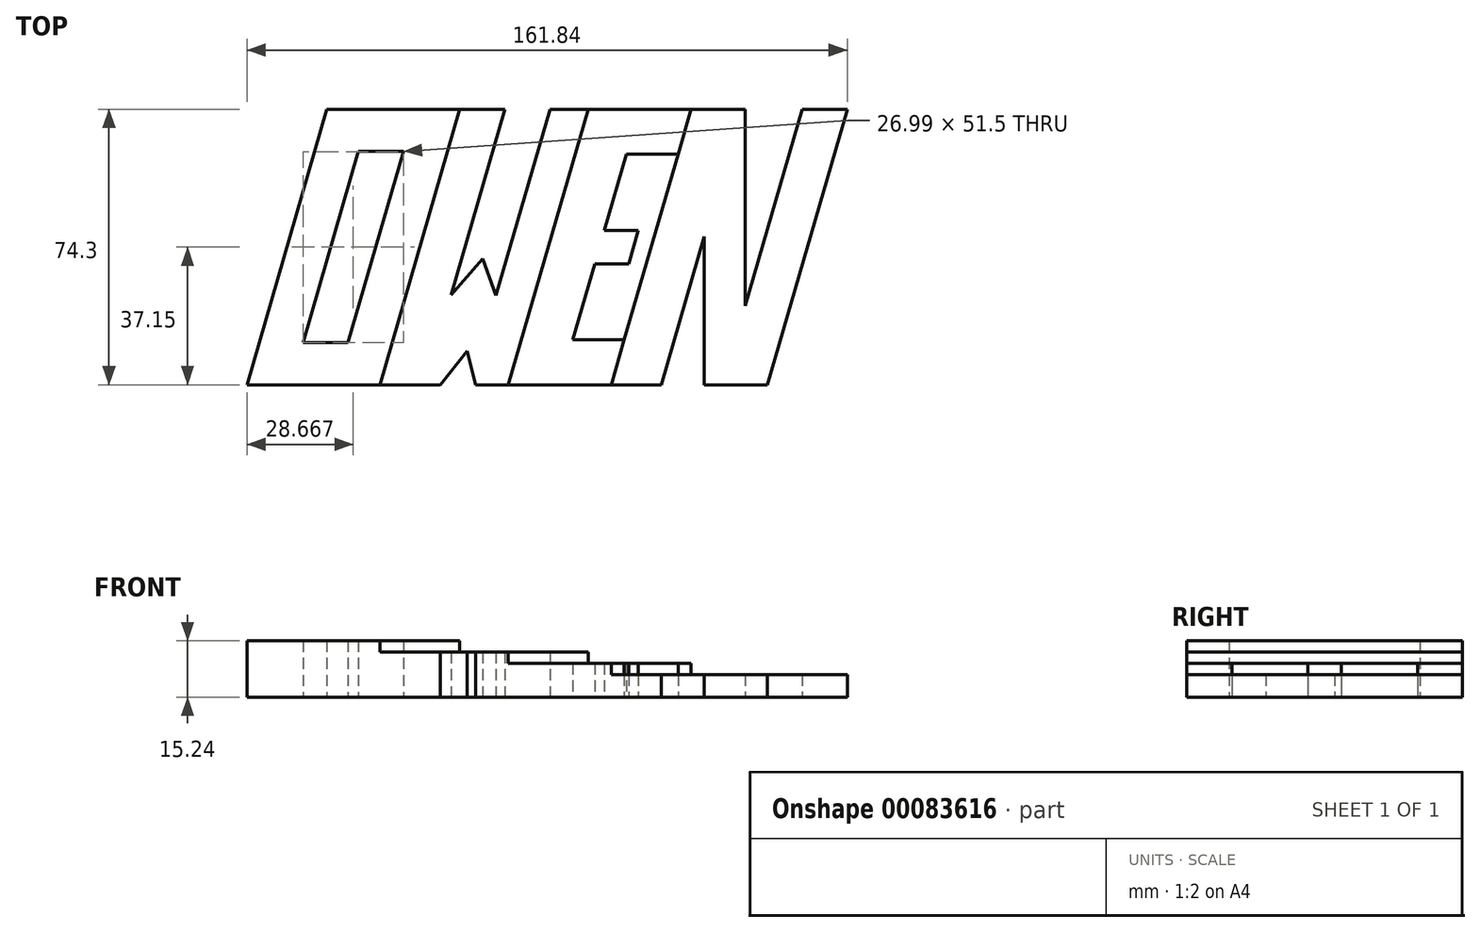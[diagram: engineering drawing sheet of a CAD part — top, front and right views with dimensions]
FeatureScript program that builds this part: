
annotation { "Feature Type Name" : "Feature", "Feature Type Description" : "" }
export const myFeature = defineFeature(function(context is Context, id is Id, definition is map)
    precondition{}
    {
        {
            var Q0;
            Q0=qCreatedBy(makeId("Top.planeOp"),FACE);
            var sketch = newSketch(context, id + "F0", { "sketchPlane" : qUnion([Q0])});
            skPoint(sketch, "E0.middle", {"position": v(0, 0) * mm});
            skLineSegment(sketch, "E1", {"start": v(-54.9, 37.15) * mm, "end": v(-76.4, -37.15) * mm});
            skLineSegment(sketch, "E2", {"start": v(-40.6, -37.15) * mm, "end": v(-19.08, 37.15) * mm});
            skLineSegment(sketch, "E3", {"start": v(-76.4, -37.15) * mm, "end": v(-40.6, -37.15) * mm});
            skLineSegment(sketch, "E4", {"start": v(-54.9, 37.15) * mm, "end": v(-19.08, 37.15) * mm});
            skLineSegment(sketch, "E5.0", {"start": v(-46.32, 25.75) * mm, "end": v(-61.24, -25.75) * mm});
            skLineSegment(sketch, "E5.1", {"start": v(-46.32, 25.75) * mm, "end": v(-34.25, 25.75) * mm});
            skLineSegment(sketch, "E5.2", {"start": v(-49.16, -25.75) * mm, "end": v(-34.25, 25.75) * mm});
            skLineSegment(sketch, "E5.3", {"start": v(-61.24, -25.75) * mm, "end": v(-49.16, -25.75) * mm});
            skLineSegment(sketch, "E6", {"start": v(-19.08, 37.15) * mm, "end": v(-6.88, 37.15) * mm});
            skLineSegment(sketch, "E7", {"start": v(-6.88, 37.15) * mm, "end": v(-21.37, -12.86) * mm});
            skLineSegment(sketch, "E8", {"start": v(-21.37, -12.86) * mm, "end": v(-12.84, -3.14) * mm});
            skLineSegment(sketch, "E9", {"start": v(-12.84, -3.14) * mm, "end": v(-9.23, -13.05) * mm});
            skLineSegment(sketch, "E10", {"start": v(-9.23, -13.05) * mm, "end": v(5.3, 37.15) * mm});
            skLineSegment(sketch, "E11", {"start": v(5.3, 37.15) * mm, "end": v(15.55, 37.15) * mm});
            skLineSegment(sketch, "E12", {"start": v(15.55, 37.15) * mm, "end": v(-5.97, -37.15) * mm});
            skLineSegment(sketch, "E13", {"start": v(-5.97, -37.15) * mm, "end": v(-14.75, -37.15) * mm});
            skLineSegment(sketch, "E14", {"start": v(-14.75, -37.15) * mm, "end": v(-17.04, -28.02) * mm});
            skLineSegment(sketch, "E15", {"start": v(-17.04, -28.02) * mm, "end": v(-24.24, -37.15) * mm});
            skLineSegment(sketch, "E16", {"start": v(-24.24, -37.15) * mm, "end": v(-40.6, -37.15) * mm});
            skLineSegment(sketch, "E17", {"start": v(15.55, 37.15) * mm, "end": v(43.3, 37.15) * mm});
            skLineSegment(sketch, "E18", {"start": v(25.93, 25.1) * mm, "end": v(19.96, 4.48) * mm});
            skLineSegment(sketch, "E19", {"start": v(25.93, 25.1) * mm, "end": v(39.8, 25.1) * mm});
            skLineSegment(sketch, "E20.bottom", {"start": v(26.52, -4.48) * mm, "end": v(17.37, -4.48) * mm});
            skLineSegment(sketch, "E20.top", {"start": v(26.52, 4.48) * mm, "end": v(19.96, 4.48) * mm});
            skLineSegment(sketch, "E21.trimOffspring", {"start": v(17.37, -4.48) * mm, "end": v(11.42, -25) * mm});
            skLineSegment(sketch, "E22", {"start": v(26.52, 4.48) * mm, "end": v(29.12, 4.48) * mm});
            skLineSegment(sketch, "E23", {"start": v(29.12, 4.48) * mm, "end": v(26.52, -4.48) * mm});
            skLineSegment(sketch, "E24", {"start": v(11.42, -25) * mm, "end": v(25.3, -25) * mm});
            skLineSegment(sketch, "E25", {"start": v(39.8, 25.1) * mm, "end": v(43.3, 37.15) * mm});
            skLineSegment(sketch, "E26", {"start": v(25.3, -25) * mm, "end": v(21.78, -37.15) * mm});
            skLineSegment(sketch, "E27", {"start": v(39.8, 25.1) * mm, "end": v(25.3, -25) * mm});
            skLineSegment(sketch, "E28", {"start": v(57.9, 37.15) * mm, "end": v(57.9, -15.78) * mm});
            skLineSegment(sketch, "E29", {"start": v(57.9, -15.78) * mm, "end": v(73.24, 37.15) * mm});
            skLineSegment(sketch, "E30", {"start": v(73.24, 37.15) * mm, "end": v(85.43, 37.15) * mm});
            skLineSegment(sketch, "E31", {"start": v(85.43, 37.15) * mm, "end": v(63.91, -37.15) * mm});
            skLineSegment(sketch, "E32", {"start": v(63.91, -37.15) * mm, "end": v(49.58, -37.15) * mm});
            skLineSegment(sketch, "E33", {"start": v(46.81, -37.15) * mm, "end": v(46.81, -7.28) * mm});
            skLineSegment(sketch, "E34", {"start": v(46.81, -7.28) * mm, "end": v(46.81, 2.77) * mm});
            skLineSegment(sketch, "E35", {"start": v(46.81, 2.77) * mm, "end": v(35.25, -37.15) * mm});
            skLineSegment(sketch, "E36", {"start": v(-5.97, -37.15) * mm, "end": v(21.78, -37.15) * mm});
            skLineSegment(sketch, "E37", {"start": v(35.25, -37.15) * mm, "end": v(21.78, -37.15) * mm});
            skLineSegment(sketch, "E38", {"start": v(46.81, -37.15) * mm, "end": v(49.58, -37.15) * mm});
            skLineSegment(sketch, "E39", {"start": v(43.3, 37.15) * mm, "end": v(57.9, 37.15) * mm});
            skLineSegment(sketch, "E40.left", {"start": v(85.43, 37.15) * mm, "end": v(85.43, -37.15) * mm});
            skLineSegment(sketch, "E41", {"start": v(-76.4, -37.15) * mm, "end": v(-76.4, 37.15) * mm});
            skLineSegment(sketch, "E42", {"start": v(-76.4, 37.15) * mm, "end": v(85.43, 37.15) * mm});
            skLineSegment(sketch, "E43", {"start": v(85.43, -37.15) * mm, "end": v(-76.4, -37.15) * mm});
            skSolve(sketch);
        }
        {
            var Q0;
            Q0=makeQuery(id+"F0.imprint","IMPRINT",FACE,{"disambiguationData":[TD([[makeQuery(id+"F0.imprint","IMPRINT",EDGE,{"derivedFrom":sQuery(id+"F0.wireOp",EDGE,"E1")}),1.0]])]});
            extrude(context, id + "F1", {"entities" : qUnion([Q0]), "depth" : 15.24 * mm});
        }
        {
            var Q0;
            Q0=makeQuery(id+"F0.imprint","IMPRINT",FACE,{"disambiguationData":[TD([[makeQuery(id+"F0.imprint","IMPRINT",EDGE,{"derivedFrom":sQuery(id+"F0.wireOp",EDGE,"E2")}),-1.0]])]});
            extrude(context, id + "F2", {"entities" : qUnion([Q0]), "operationType" : NewBodyOperationType.ADD, "depth" : 12.2 * mm});
        }
        {
            var Q0;
            Q0=makeQuery(id+"F0.imprint","IMPRINT",FACE,{"disambiguationData":[TD([[makeQuery(id+"F0.imprint","IMPRINT",EDGE,{"derivedFrom":sQuery(id+"F0.wireOp",EDGE,"E12")}),1.0]])]});
            extrude(context, id + "F3", {"entities" : qUnion([Q0]), "operationType" : NewBodyOperationType.ADD, "depth" : 9.14 * mm});
        }
        {
            var Q0;
            Q0=makeQuery(id+"F0.imprint","IMPRINT",FACE,{"disambiguationData":[TD([[makeQuery(id+"F0.imprint","IMPRINT",EDGE,{"derivedFrom":sQuery(id+"F0.wireOp",EDGE,"E25")}),-1.0]])]});
            extrude(context, id + "F4", {"entities" : qUnion([Q0]), "operationType" : NewBodyOperationType.ADD, "depth" : 6.1 * mm});
        }
    });
